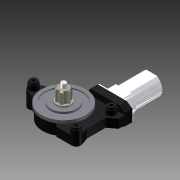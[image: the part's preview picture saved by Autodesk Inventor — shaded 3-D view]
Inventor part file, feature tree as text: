
AUTODESK INVENTOR PART (.ipt)
format: ipt  version: 2011 (Build 150239000, 239)  size: 438,784 bytes
history: native  units: mm
features: extrude x20, sketch x14, plane x4, chamfer x3, projected_geometry x3, pattern_circular x2, revolve x1, hole x1, other x1, fillet x1
ambient origin geometry x8: Origin, YZ Plane, XZ Plane, XY Plane, X Axis, Y Axis, Z Axis, Center Point
bodies: Solid1 (feature_tree)
feature tree (50):
  sketch  "Sketch1"  dims[d0=72.0mm d1=4.8mm d2=0.0mm]
  extrude  "Extrusion1"  Depth=4.8mm TaperAngle=0.0deg
  extrude  "Extrusion2"  Depth=42.0mm
  extrude  "Extrusion3"  Depth=1.9mm TaperAngle=0.0deg
  extrude  "Extrusion4"  Depth=23.8mm
  extrude  "Extrusion5"  Depth=16.4mm
  extrude  "Extrusion6"  Depth=8.0mm
  extrude  "Extrusion7"  Depth=19.9mm
  chamfer  "Chamfer1"  Distance=6.7mm
  pattern_circular  "Circular Pattern1"  Count=6 Angle=360.0deg
  sketch  "Sketch6"  dims[d14=18.0mm d15=0.0mm d16=8.0mm]
  extrude  "Extrusion8"  Depth=14.2mm
  plane  "Work Plane1"
  extrude  "Extrusion9"  Depth=56.76mm
  extrude  "Extrusion10"  Depth=37.0mm
  extrude  "Extrusion11"  Depth=25.0mm
  revolve  "Revolution1"  [1 undecoded]
  extrude  "Extrusion20"  Depth=30.5mm
  pattern_circular  "Circular Pattern2"  [2 undecoded]
  extrude  "Extrusion12"  Depth=15.0mm
  extrude  "Extrusion13"  Depth=18.6mm TaperAngle=0.0deg
  hole  "Hole2"  [1 undecoded]
  plane  "Work Plane4"
  extrude  "Extrusion19"  Depth=17.0mm TaperAngle=0.0deg
  other  "Work Axis1"
  extrude  "Extrusion14"  Depth=14.0mm TaperAngle=0.0deg
  chamfer  "Chamfer2"  Distance=19.5mm
  chamfer  "Chamfer3"  Distance=3.0mm
  fillet  "Fillet1"  Radius=3.0mm
  sketch  "Sketch13"  dims[d31=101.5mm d32=56.76mm]
  extrude  "Extrusion15"  Depth=11.9mm
  extrude  "Extrusion16"  Depth=3.0mm TaperAngle=0.0deg
  extrude  "Extrusion17"  [1 undecoded]
  extrude  "Extrusion18"  Depth=31.0mm
  sketch  "Sketch2"  dims[d3=60.0mm d4=42.0mm]
  sketch  "Sketch3"  dims[d5=25.8mm d6=1.9mm d7=0.0mm]
  sketch  "Sketch4"  dims[d8=1.2mm d9=0.0mm d10=23.8mm]
  sketch  "Sketch5"  dims[d11=3.0mm d12=0.0mm d13=16.4mm]
  sketch  "Sketch7"  dims[d17=6.7mm d18=0.0mm d19=19.9mm]
  sketch  "Sketch10"  dims[d20=4.0mm d21=6.7mm d22=0.0mm]
  projected_geometry  "Projected Loop4"
  sketch  "Sketch11"  dims[d23=1.75mm d24=2.0mm d25=45.0deg d26=60.0mm d27=360.0deg]
  projected_geometry  "Projected Loop5"
  projected_geometry  "Projected Loop6"
  plane  "Work Plane2"
  plane  "Work Plane3"
  sketch  "Sketch12"  dims[d29=68.0mm d30=14.2mm]
  sketch  "Sketch14"  dims[d33=16.3mm d34=37.0mm]
  sketch  "Sketch15"  dims[d35=135.0deg d36=25.0mm]
  sketch  "Sketch16"  dims[d37=10.0mm d38=63.0mm d39=30.5mm d40=13.2mm d41=15.0mm d42=18.6mm d43=0.0mm d44=6.0mm d45=17.0mm d46=0.0mm d47=14.0mm d48=0.0mm d49=19.5mm d50=3.0mm d51=0.0mm d52=3.0mm d53=0.0mm d61=11.9mm d62=3.0mm d63=0.0mm d64=5.0mm d65=6.0mm d66=4.0mm d67=2.0mm d68=90.0deg d69=8.0mm d70=20.594885mm d71=-17.0mm d73=31.0mm d74=12.0mm d75=0.0mm d76=40.0mm d78=6.0mm d79=9.0mm d80=45.0deg d81=6.0mm d82=9.0mm d83=45.0deg d84=6.5mm d85=34.9mm d86=19.95mm d88=3.75mm d89=17.45mm d90=3.0mm d91=10.0mm d92=2.0mm d93=0.0mm d94=15.0mm d95=0.0mm d96=60.0mm d97=0.0mm d98=67.0mm d99=0.0mm d100=0.2mm d101=3.55mm d102=-36.2mm d103=67.0mm d104=0.0mm d106=19.6mm d107=3.8mm d108=90.0deg d109=30.0deg d110=1.0mm d111=19.0mm d112=2.0mm d113=1.0mm d114=4.5mm d115=0.0mm d116=120.0mm d117=360.0deg]
note: 5 required parameter values undecoded (feature->parameter linkage not recoverable at this tier; creation-order binding heuristic only, values carry confidence <= 0.55)